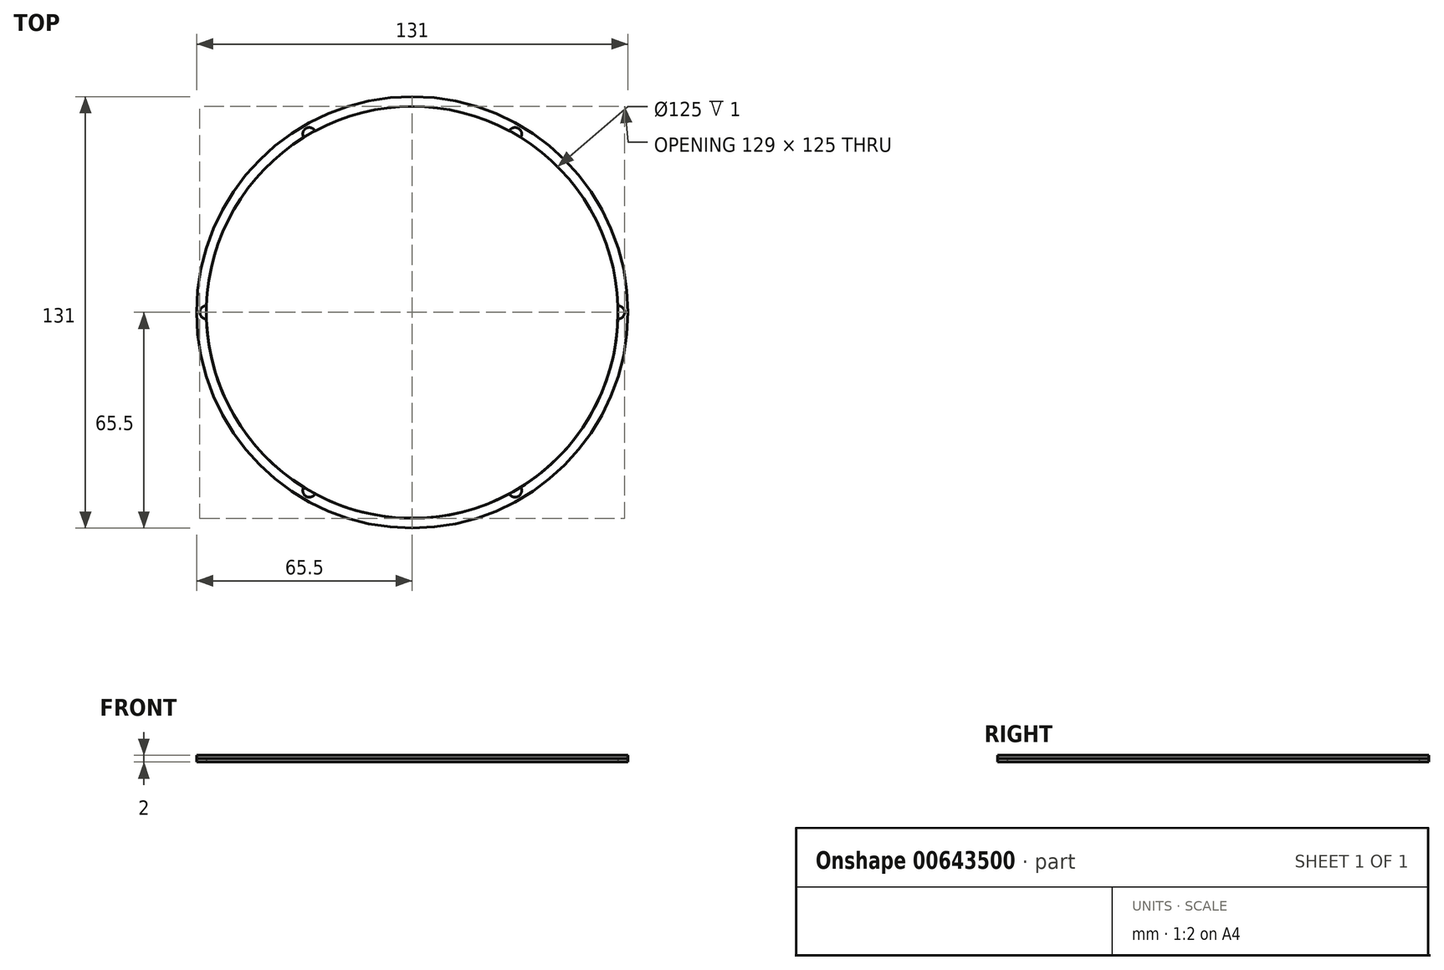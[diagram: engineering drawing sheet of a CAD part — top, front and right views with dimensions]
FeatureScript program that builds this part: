
annotation { "Feature Type Name" : "Feature", "Feature Type Description" : "" }
export const myFeature = defineFeature(function(context is Context, id is Id, definition is map)
    precondition{}
    {
        {
            var Q0;
            Q0=qCreatedBy(makeId("Top.planeOp"),FACE);
            var sketch = newSketch(context, id + "F0", { "sketchPlane" : qUnion([Q0])});
            skCircle(sketch, "E0", {"center": v(0, 0) * mm, "radius": 62.5 * mm});
            skCircle(sketch, "E1", {"center": v(0, 0) * mm, "radius": 65.5 * mm});
            skLineSegment(sketch, "E2", {"start": v(-65.5, 0) * mm, "end": v(65.5, 0) * mm, "construction": true});
            skLineSegment(sketch, "E3", {"start": v(-37.5, 64.95) * mm, "end": v(37.5, -64.95) * mm, "construction": true});
            skLineSegment(sketch, "E4", {"start": v(37.5, 64.95) * mm, "end": v(-37.5, -64.95) * mm, "construction": true});
            skArc(sketch, "E5", {"start": v(-32.97, 53.1) * mm, "mid": v(-32.25, 55.86) * mm, "end": v(-29.5, 55.1) * mm});
            skArc(sketch, "E6.1.0", {"start": v(-62.47, -2) * mm, "mid": v(-64.5, 0) * mm, "end": v(-62.47, 2) * mm});
            skArc(sketch, "E6.2.0", {"start": v(-29.5, -55.1) * mm, "mid": v(-32.25, -55.86) * mm, "end": v(-32.97, -53.1) * mm});
            skArc(sketch, "E7.2.3.0", {"start": v(32.97, -53.1) * mm, "mid": v(32.25, -55.86) * mm, "end": v(29.5, -55.1) * mm});
            skArc(sketch, "E7.2.4.0", {"start": v(62.47, 2) * mm, "mid": v(64.5, 0) * mm, "end": v(62.47, -2) * mm});
            skArc(sketch, "E7.2.5.0", {"start": v(29.5, 55.1) * mm, "mid": v(32.25, 55.86) * mm, "end": v(32.97, 53.1) * mm});
            skSolve(sketch);
        }
        {
            var Q0;
            Q0 = qSketchRegion(id + "F0", true);
            extrude(context, id + "F1", {"entities" : qUnion([Q0]), "depth" : 2 * mm, "offsetDistance" : 25 * mm});
        }
        {
            var Q0;
            Q0=qCreatedBy(makeId("Top.planeOp"),FACE);
            var sketch = newSketch(context, id + "F2", { "sketchPlane" : qUnion([Q0])});
            skCircle(sketch, "E8", {"center": v(0, 0) * mm, "radius": 62.5 * mm});
            skCircle(sketch, "E9", {"center": v(0, 0) * mm, "radius": 65.5 * mm});
            skSolve(sketch);
        }
        {
            var Q0;
            Q0 = qSketchRegion(id + "F2", true);
            extrude(context, id + "F3", {"entities" : qUnion([Q0]), "depth" : 1 * mm, "offsetDistance" : 25 * mm});
        }
    });
